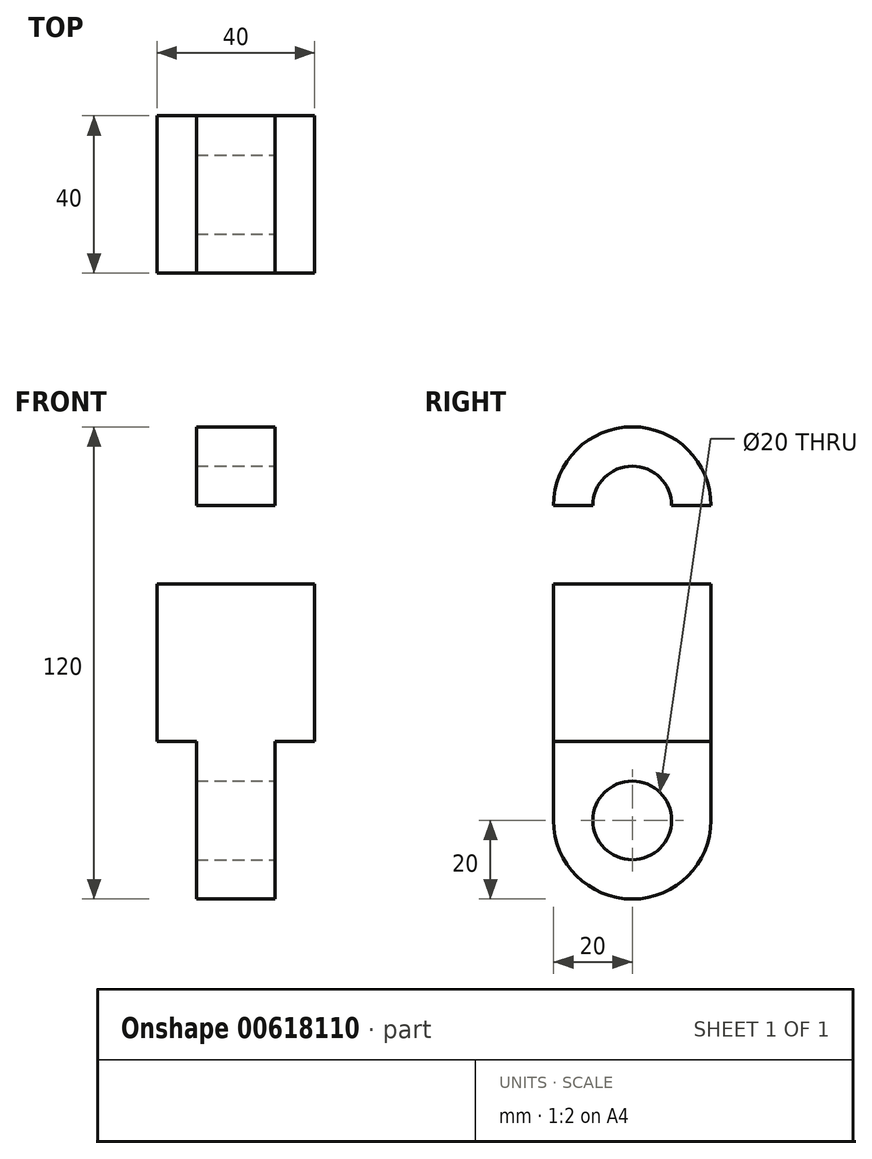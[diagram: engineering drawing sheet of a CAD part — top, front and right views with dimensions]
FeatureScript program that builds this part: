
annotation { "Feature Type Name" : "Feature", "Feature Type Description" : "" }
export const myFeature = defineFeature(function(context is Context, id is Id, definition is map)
    precondition{}
    {
        {
            var Q0;
            Q0=qCreatedBy(makeId("Front.planeOp"),FACE);
            var sketch = newSketch(context, id + "F0", { "sketchPlane" : qUnion([Q0])});
            skLineSegment(sketch, "E0.bottom", {"start": v(20, -20) * mm, "end": v(0, -20) * mm});
            skLineSegment(sketch, "E0.top", {"start": v(20, 20) * mm, "end": v(-20, 20) * mm});
            skLineSegment(sketch, "E0.left", {"start": v(20, -20) * mm, "end": v(20, 20) * mm});
            skLineSegment(sketch, "E0.right", {"start": v(-20, -20) * mm, "end": v(-20, 20) * mm});
            skPoint(sketch, "E0.middle", {"position": v(0, 0) * mm});
            skLineSegment(sketch, "E1.bottom", {"start": v(10, 20) * mm, "end": v(-10, 20) * mm});
            skLineSegment(sketch, "E1.top", {"start": v(10, 40) * mm, "end": v(-10, 40) * mm});
            skLineSegment(sketch, "E1.left", {"start": v(10, 20) * mm, "end": v(10, 40) * mm});
            skLineSegment(sketch, "E1.right", {"start": v(-10, 20) * mm, "end": v(-10, 40) * mm});
            skPoint(sketch, "E1.middle", {"position": v(0, 30) * mm});
            skLineSegment(sketch, "E2.top", {"start": v(10, -40) * mm, "end": v(-10, -40) * mm});
            skLineSegment(sketch, "E2.left", {"start": v(10, -20) * mm, "end": v(10, -40) * mm});
            skLineSegment(sketch, "E2.right", {"start": v(-10, -20) * mm, "end": v(-10, -40) * mm});
            skPoint(sketch, "E2.middle", {"position": v(0, -30) * mm});
            skPoint(sketch, "E2.middle.positionSnap0", {"position": v(0, -20) * mm});
            skPoint(sketch, "E2.centerSnap0", {"position": v(0, -20) * mm});
            skLineSegment(sketch, "E3.top", {"start": v(10, 60) * mm, "end": v(-10, 60) * mm});
            skLineSegment(sketch, "E3.left", {"start": v(10, 40) * mm, "end": v(10, 60) * mm});
            skLineSegment(sketch, "E3.right", {"start": v(-10, 40) * mm, "end": v(-10, 60) * mm});
            skPoint(sketch, "E3.middle", {"position": v(0, 50) * mm});
            skLineSegment(sketch, "E4.top", {"start": v(10, -60) * mm, "end": v(-10, -60) * mm});
            skLineSegment(sketch, "E4.left", {"start": v(10, -40) * mm, "end": v(10, -60) * mm});
            skLineSegment(sketch, "E4.right", {"start": v(-10, -40) * mm, "end": v(-10, -60) * mm});
            skPoint(sketch, "E4.middle", {"position": v(0, -50) * mm});
            skLineSegment(sketch, "E5.trimOffspring", {"start": v(-10, -20) * mm, "end": v(-20, -20) * mm});
            skSolve(sketch);
        }
        {
            var Q0;
            {var subQ0=sQuery(id+"F0.wireOp",EDGE,"E0.left");Q0=makeQuery(id+"F0.imprint","IMPRINT",FACE,{"disambiguationData":[TD([[makeQuery(id+"F0.imprint","IMPRINT",EDGE,{"derivedFrom":subQ0}),1.0]])]});}
            var Q1;
            Q1=makeQuery(id+"F0.imprint","IMPRINT",FACE,{"disambiguationData":[TD([[makeQuery(id+"F0.imprint","IMPRINT",EDGE,{"derivedFrom":sQuery(id+"F0.wireOp",EDGE,"E1.bottom")}),-1.0]])]});
            var Q2;
            Q2=makeQuery(id+"F0.imprint","IMPRINT",FACE,{"disambiguationData":[TD([[makeQuery(id+"F0.imprint","IMPRINT",EDGE,{"derivedFrom":sQuery(id+"F0.wireOp",EDGE,"E1.top")}),-1.0]])]});
            var Q3;
            Q3=makeQuery(id+"F0.imprint","IMPRINT",FACE,{"disambiguationData":[TD([[makeQuery(id+"F0.imprint","IMPRINT",EDGE,{"derivedFrom":sQuery(id+"F0.wireOp",EDGE,"E2.top")}),1.0]])]});
            extrude(context, id + "F1", {"entities" : qUnion([Q0, Q1, Q2, Q3]), "depth" : 40 * mm, "offsetDistance" : 25 * mm});
        }
        {
            var Q0;
            Q0=makeQuery(id+"F1.opExtrude","CAP_EDGE",EDGE,{"disambiguationData":[OSD([sQuery(id+"F0.wireOp",EDGE,"E3.top")])],"isStart":false});
            var Q1;
            Q1=makeQuery(id+"F1.opExtrude","CAP_EDGE",EDGE,{"disambiguationData":[OSD([sQuery(id+"F0.wireOp",EDGE,"E3.top")])],"isStart":true});
            var Q2;
            Q2=makeQuery(id+"F1.opExtrude","CAP_EDGE",EDGE,{"disambiguationData":[OSD([sQuery(id+"F0.wireOp",EDGE,"E4.top")])],"isStart":false});
            var Q3;
            Q3=makeQuery(id+"F1.opExtrude","CAP_EDGE",EDGE,{"disambiguationData":[OSD([sQuery(id+"F0.wireOp",EDGE,"E4.top")])],"isStart":true});
            fillet(context, id + "F2", {"entities" : qUnion([Q0, Q1, Q2, Q3]), "radius" : 20 * mm, "tangentPropagation" : true, "allowEdgeOverflow" : false});
        }
        {
            var Q0;
            Q0=makeQuery(id+"F1.opExtrude","SWEPT_FACE",FACE,{"disambiguationData":[OSD([sQuery(id+"F0.wireOp",EDGE,"E1.left"),sQuery(id+"F0.wireOp",EDGE,"E3.left")])]});
            var sketch = newSketch(context, id + "F3", { "sketchPlane" : qUnion([Q0])});
            skCircle(sketch, "E6", {"center": v(-20, 40) * mm, "radius": 10 * mm});
            skSolve(sketch);
        }
        {
            var Q0;
            Q0=makeQuery(id+"F1.opExtrude","SWEPT_FACE",FACE,{"disambiguationData":[OSD([sQuery(id+"F0.wireOp",EDGE,"E2.left"),sQuery(id+"F0.wireOp",EDGE,"E4.left")])]});
            var sketch = newSketch(context, id + "F4", { "sketchPlane" : qUnion([Q0])});
            skCircle(sketch, "E7", {"center": v(-20, -40) * mm, "radius": 10 * mm});
            skSolve(sketch);
        }
        {
            var Q0;
            Q0=makeQuery(id+"F3.imprint","IMPRINT",FACE,{"disambiguationData":[TD([[makeQuery(id+"F3.imprint","IMPRINT",EDGE,{"derivedFrom":sQuery(id+"F3.wireOp",EDGE,"E6")}),1.0]])]});
            extrude(context, id + "F5", {"entities" : qUnion([Q0]), "operationType" : NewBodyOperationType.REMOVE, "endBound" : BoundingType.UP_TO_NEXT, "oppositeDirection" : true, "depth" : 25 * mm, "offsetDistance" : 25 * mm});
        }
        {
            var Q0;
            Q0=makeQuery(id+"F4.imprint","IMPRINT",FACE,{"disambiguationData":[TD([[makeQuery(id+"F4.imprint","IMPRINT",EDGE,{"derivedFrom":sQuery(id+"F4.wireOp",EDGE,"E7")}),1.0]])]});
            extrude(context, id + "F6", {"entities" : qUnion([Q0]), "operationType" : NewBodyOperationType.REMOVE, "endBound" : BoundingType.UP_TO_NEXT, "oppositeDirection" : true, "depth" : 25 * mm, "offsetDistance" : 25 * mm});
        }
    });
